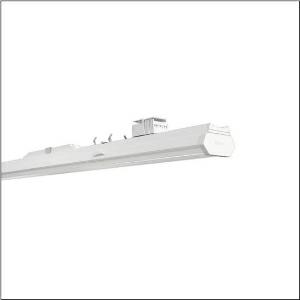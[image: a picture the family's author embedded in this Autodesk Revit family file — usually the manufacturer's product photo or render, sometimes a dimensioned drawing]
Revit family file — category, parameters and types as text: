
# Revit family: licross_11_protected_mo_51tp11dn495g
name_source: partatom
category: Lighting Fixtures
units: mm (PartAtom-declared; Revit-internal decimal feet)

## family parameters
Cut with Voids When Loaded = No
Host = Face
Light Source = No
Part Type = Normal
Room Calculation Point = No
Round Connector Dimension = Use Diameter
Shared = No

## types (1)
- --- (1 x LED, 9930 lm, 57.1 W, 4000K)
    Apparent Load = 57 VA
    CIE Flux Codes = 83 94 98 100 100
    Color Rendering = 80
    Color Temperature = 4000K
    Default Elevation = 1800 mm
    Description = Licross 11 Protected MO, luminaire insert, of sheet steel, galvanised, coil coated, white, length: 1.500mm, width: 90mm, height: 101mm, LED rated luminous flux: 9.980lm, light colour: 840, SDCM (Standard Deviation of Colour Matching)MacAdam ≤ 2 SDCM (initial), control gear: DALI 2, with plug, 5-pole, with phase selection, mains connection: 220..240V, AC, 50/60Hz, rated input power: 57W, internal wiring halogen-free, primary light control with lens, of plastic, primary optical cover: cover, of PMMA, light emission: direct distribution, primary light characteristic: symmetric, protection rating (complete): IP64, insulation class (complete): insulation class I (protective earthing), certification: CE, ENEC, VDE, UKCA, protection symbol: D if used in an environment with conductive dust loads with corresponding accessories, impact resistance: IK06, permissible ambient temperature for indoor applications: -25..+35°C, corresponds to IFS (International Featured Standards) requirements for safety and quality in the food industry, reducing of maximum allowable ambient temperature of 5°C with ceiling mounting, LABS conformity tested according to VDMA 24364:2018-05, The light source and the operating device comply with the requirements of the Ecodesign Regulation (EU) 2019/2020 and are replaceable in accordance with this regulation, packaging unit: 1 piece
    Height = 92 mm
    Lamp = 1 x LED
    Lamp Light Flux = 9930 lm
    Lamp Power = 57.1 W
    Lamp count = 1
    Length = 1500 mm
    Luminous efficacy = 174 lm/W
    Manufacturer = Siteco
    ModVariant = No
    Model = 51TP11DN495G
    Mounting Place = Ceiling
    Mounting Type = Pendant
    Number of Poles = 1
    OnlyDefault = Yes
    Power Factor = 1
    Product Name = Licross 11 Protected MO
    Product group = luminaire insert | ceiling pendant
    ProductGroupID = 901
    Protection Class = Protection class I
    Protection Degree = IP 64
    RLX_Detail_Level = 1
    RLX_Emergency_Light_Flux = 0 lm
    RLX_Emergency_Type = 0
    RLX_Emergency_Type_DB = No
    RlxData = <blob elided: 24413 chars, md5=fe627104>
    Socket = socket
    Standby Power = 0 W
    System Light Flux = 9930 lm
    System Power = 57 W
    Type Comments = factory setting: luminous flux: 100 % | dim-lin: 254 | 378 mA
    Type Image = l_1256148.jpg
    URL = http://relux.com
    VarID = @adj_102515
    Voltage = 0 V
    Weight = 0.00 kg
    Width = 88 mm

## geometry (parser evidence)
native form markers: Blend x4, Sweep x12
no freeform markers — native parametric forms only
